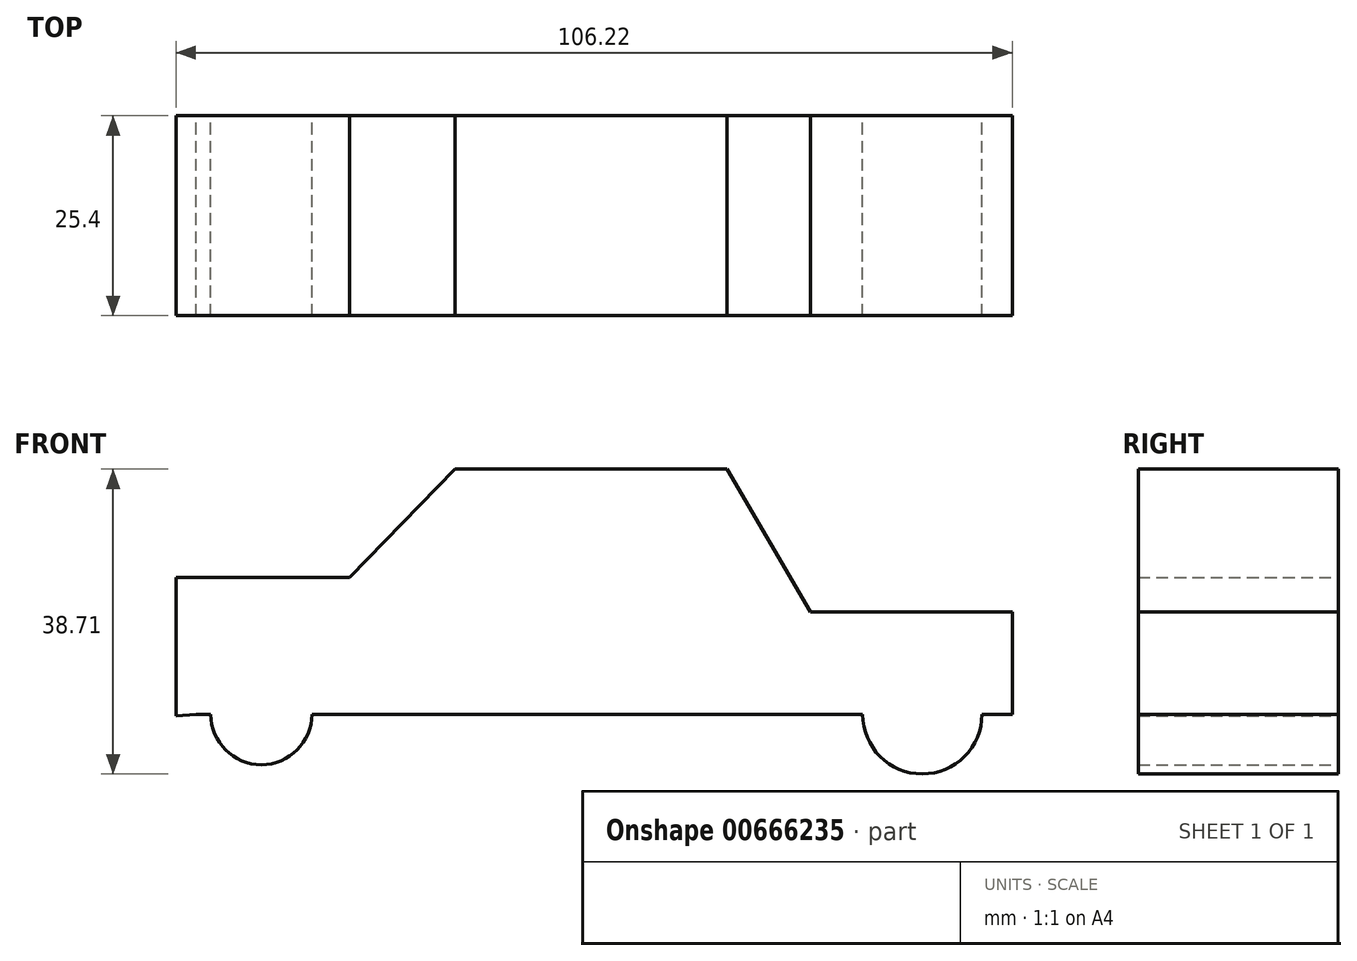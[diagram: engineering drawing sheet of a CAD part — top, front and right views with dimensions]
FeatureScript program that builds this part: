
annotation { "Feature Type Name" : "Feature", "Feature Type Description" : "" }
export const myFeature = defineFeature(function(context is Context, id is Id, definition is map)
    precondition{}
    {
        {
            var Q0;
            Q0=qCreatedBy(makeId("Front.planeOp"),FACE);
            var sketch = newSketch(context, id + "F0", { "sketchPlane" : qUnion([Q0])});
            skLineSegment(sketch, "E0", {"start": v(-58.43, -25.32) * mm, "end": v(45.23, -25.32) * mm});
            skLineSegment(sketch, "E1", {"start": v(45.23, -25.32) * mm, "end": v(45.23, -12.32) * mm});
            skLineSegment(sketch, "E2", {"start": v(45.23, -12.32) * mm, "end": v(19.6, -12.32) * mm});
            skLineSegment(sketch, "E3", {"start": v(19.6, -12.32) * mm, "end": v(8.97, 5.81) * mm});
            skLineSegment(sketch, "E4", {"start": v(8.97, 5.81) * mm, "end": v(-25.52, 5.81) * mm});
            skLineSegment(sketch, "E5", {"start": v(-25.52, 5.81) * mm, "end": v(-38.92, -7.98) * mm});
            skLineSegment(sketch, "E6", {"start": v(-38.92, -7.98) * mm, "end": v(-61, -7.98) * mm});
            skLineSegment(sketch, "E7", {"start": v(-61, -7.98) * mm, "end": v(-61, -25.52) * mm});
            skLineSegment(sketch, "E8", {"start": v(-61, -25.52) * mm, "end": v(-58.43, -25.32) * mm});
            skCircle(sketch, "E9", {"center": v(-50.15, -25.32) * mm, "radius": 6.42 * mm});
            skCircle(sketch, "E10", {"center": v(33.8, -25.32) * mm, "radius": 7.58 * mm});
            skLineSegment(sketch, "E11", {"start": v(-61, -16.75) * mm, "end": v(-38.92, -7.98) * mm});
            skLineSegment(sketch, "E12", {"start": v(-61, -7.98) * mm, "end": v(-61, -16.75) * mm});
            skSolve(sketch);
        }
        {
            var Q0;
            Q0 = qSketchRegion(id + "F0", true);
            extrude(context, id + "F1", {"entities" : qUnion([Q0]), "depth" : 25.4 * mm, "offsetDistance" : 25.4 * mm});
        }
    });
